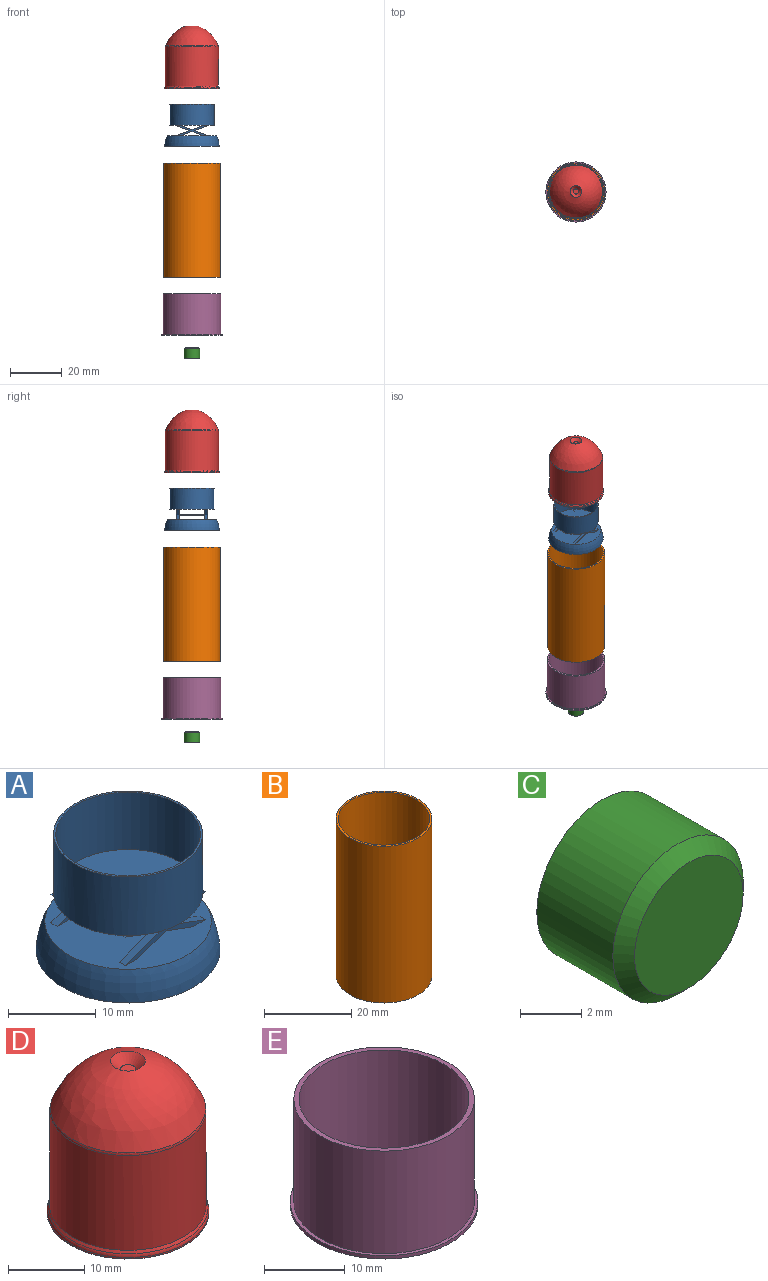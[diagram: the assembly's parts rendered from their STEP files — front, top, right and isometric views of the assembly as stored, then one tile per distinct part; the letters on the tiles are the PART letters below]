
ASSEMBLY  parts=5 mates=4
PART A: 40 faces, bbox 21x21x16.2 mm
  f0: plane 17.01x17.01mm, normal (0,0,-1), area 219.3mm2, adj f1,f6,f7,f8,f9,f10,f11,f12
  f1: cylinder r=8.5mm len=17mm, axis (0,0,1), area 437.9mm2, adj f0,f2,f3,f4,f5,f37
  f2: plane 0.45x0.43mm, normal (0,0,1), area 0.1mm2, adj f1,f8,f21
  f3: plane 0.45x0.43mm, normal (0,0,1), area 0.1mm2, adj f1,f8,f18
  f4: plane 0.46x0.43mm, normal (0,0,1), area 0.1mm2, adj f1,f12,f25
  f5: plane 0.45x0.43mm, normal (0,0,1), area 0.1mm2, adj f1,f12,f26
  f6: plane 4.43x1.63mm, normal (0.34,0,0.94), area 4.7mm2, adj f0,f7,f8,f9
  f7: plane 4.43x1.63mm, normal (-0.34,0,0.94), area 4.7mm2, adj f0,f6,f8,f9
  f8: plane 12.89x4mm, normal (0,1,0), area 15.2mm2, adj f0,f2,f3,f6,f7,f14,f17,f18
  f9: plane 12.9x4mm, normal (0,-1,0), area 14.8mm2, adj f0,f6,f7,f14,f17,f18,f19,f20
  f10: plane 4.43x1.63mm, normal (-0.34,0,0.94), area 4.7mm2, adj f0,f11,f12,f13
  f11: plane 4.43x1.63mm, normal (0.34,0,0.94), area 4.7mm2, adj f0,f10,f12,f13
  f12: plane 12.89x4mm, normal (0,-1,0), area 15.2mm2, adj f0,f4,f5,f10,f11,f14,f25,f26
  f13: plane 12.89x4mm, normal (0,1,0), area 14.8mm2, adj f0,f10,f11,f14,f25,f26,f27,f28
  f14: plane 19x18.95mm, normal (0,0,1), area 275.5mm2, adj f8,f9,f12,f13,f16,f17,f19,f20
  f15: plane 21x21mm, normal (0,0,-1), area 77.5mm2, adj f16,f23,f24,f35
  f16: torus R=0.21mm, axis (0,0,1), area 264.3mm2, adj f14,f15,f24
  f17: plane 5.45x2mm, normal (-0.34,0,0.94), area 5.8mm2, adj f8,f9,f14,f18
  f18: plane 5.46x2.01mm, normal (-0.34,0,-0.94), area 5.8mm2, adj f0,f3,f8,f9,f17
  f19: plane 4.45x1.63mm, normal (-0.34,0,-0.94), area 4.7mm2, adj f8,f9,f14,f20
  f20: plane 4.45x1.63mm, normal (0.34,0,-0.94), area 4.7mm2, adj f8,f9,f14,f19
  f21: plane 5.45x2mm, normal (0.34,0,-0.94), area 5.8mm2, adj f0,f2,f8,f9,f22
  f22: plane 5.45x2mm, normal (0.34,0,0.94), area 5.8mm2, adj f8,f9,f14,f21
  f23: plane 4x2mm, normal (1,0,0), area 8mm2, adj f14,f15,f24
  f24: cylinder r=9.5mm len=4mm, axis (0,0,1), area 8mm2, adj f15,f16,f23
  f25: plane 5.46x2.01mm, normal (0.34,0,-0.94), area 5.8mm2, adj f0,f4,f12,f13,f30
  f26: plane 5.45x2mm, normal (-0.34,0,-0.94), area 5.8mm2, adj f0,f5,f12,f13,f27
  f27: plane 5.45x2mm, normal (-0.34,0,0.94), area 5.8mm2, adj f12,f13,f14,f26
  f28: plane 4.45x1.63mm, normal (0.34,0,-0.94), area 4.7mm2, adj f12,f13,f14,f29
  f29: plane 4.45x1.63mm, normal (-0.34,0,-0.94), area 4.7mm2, adj f12,f13,f14,f28
  f30: plane 5.45x2mm, normal (0.34,0,0.94), area 5.8mm2, adj f12,f13,f14,f25
  f31: plane 10x1.01mm, normal (0,0,-1), area 10.1mm2, adj f9,f13,f32,f34
  f32: plane 10x0.45mm, normal (1,0,0), area 4.5mm2, adj f9,f13,f31,f33
  f33: plane 10x1.01mm, normal (0,0,1), area 10.1mm2, adj f9,f13,f32,f34
  f34: plane 10x0.45mm, normal (-1,0,0), area 4.5mm2, adj f9,f13,f31,f33
  f35: cylinder r=9.25mm len=18.5mm, axis (0,0,-1), area 116.2mm2, adj f15,f36
  f36: plane 18.5x18.5mm, normal (0,0,-1), area 268.8mm2, adj f35
  f37: plane 17x17mm, normal (0,0,1), area 13.2mm2, adj f1,f38
  f38: cylinder r=8.25mm len=16.5mm, axis (0,0,1), area 414.7mm2, adj f37,f39
  f39: plane 16.5x16.5mm, normal (0,0,1), area 213.8mm2, adj f38
PART B: 4 faces, bbox 22x22x44 mm
  f0: cylinder r=11mm len=44mm, axis (0,0,-1), area 3041.1mm2, adj f1,f2
  f1: plane 22x22mm, normal (0,0,1), area 33.8mm2, adj f0,f3
  f2: plane 22x22mm, normal (0,0,-1), area 33.8mm2, adj f0,f3
  f3: cylinder r=10.5mm len=44mm, axis (0,0,1), area 2902.8mm2, adj f1,f2
PART C: 4 faces, bbox 6x4x6 mm
  f0: cylinder r=3mm len=6mm, axis (0,1,0), area 66mm2, adj f2,f3
  f1: plane 5x5mm, normal (0,-1,0), area 19.6mm2, adj f2
  f2: cone r=2.5mm half-angle=45deg, axis (0,1,0), area 12.2mm2, adj f0,f1
  f3: plane 6x6mm, normal (0,1,0), area 28.3mm2, adj f0
PART D: 9 faces, bbox 22.9x22.9x24.3 mm
  f0: plane 21.2x21.2mm, normal (0,0,-1), area 353mm2, adj f1
  f1: cylinder r=10.6mm len=21.2mm, axis (0,0,-1), area 15.5mm2, adj f0,f5
  f2: cone r=10.6mm half-angle=30deg, axis (0,0,-1), area 30.2mm2, adj f3,f5
  f3: cylinder r=10.23mm len=20.47mm, axis (0,0,-1), area 978.3mm2, adj f2,f6
  f4: revolved ~20.34x20.34mm, area 481.3mm2, adj f6,f8
  f5: torus R=9.6mm, axis (0,0,1), area 34.7mm2, adj f1,f2
  f6: torus R=9.23mm, axis (0,0,1), area 23.5mm2, adj f3,f4
  f7: plane 2x2mm, normal (0,0,1), area 3.1mm2, adj f8
  f8: cone r=3mm half-angle=45deg, axis (0,0,1), area 18.4mm2, adj f4,f7
PART E: 8 faces, bbox 23.2x23.2x16 mm
  f0: plane 23.2x23.2mm, normal (0,0,-1), area 372.5mm2, adj f1,f7
  f1: cylinder r=11.6mm len=23.2mm, axis (0,0,1), area 36.4mm2, adj f0,f2
  f2: plane 23.2x23.2mm, normal (0,0,1), area 32.2mm2, adj f1,f3
  f3: cylinder r=11.15mm len=22.3mm, axis (0,0,1), area 1085.9mm2, adj f2,f4
  f4: plane 22.3x22.3mm, normal (0,0,1), area 44.2mm2, adj f3,f5
  f5: cylinder r=10.5mm len=21mm, axis (0,0,1), area 989.6mm2, adj f4,f6
  f6: plane 21x21mm, normal (0,0,1), area 318.1mm2, adj f5,f7
  f7: torus R=4mm, axis (0,0,1), area 33.2mm2, adj f0,f6
PLACE A t=(-39.69,109.65,49.17)mm
PLACE B rot(axis=(1,0,0),180deg) t=(-39.69,109.65,38.58)mm
PLACE C rot(axis=(-1,0,0),90deg) t=(-39.69,109.65,-33.51)mm
PLACE D t=(-39.69,109.65,77.33)mm
PLACE E t=(-39.69,109.65,-8.51)mm
MATE cylindrical D.f1 <-> A.f38  axis (0,0,-1) through (-39.69,109.65,67.23)mm
MATE cylindrical B.f3 <-> E.f5  axis (0,0,-1) through (-39.69,109.65,-5.42)mm
MATE cylindrical A.f35 <-> E.f5  axis (0,0,-1) through (-39.69,109.65,45.17)mm
MATE cylindrical C.f0 <-> E.f7  axis (0,0,-1) through (-39.69,109.65,-36.51)mm
